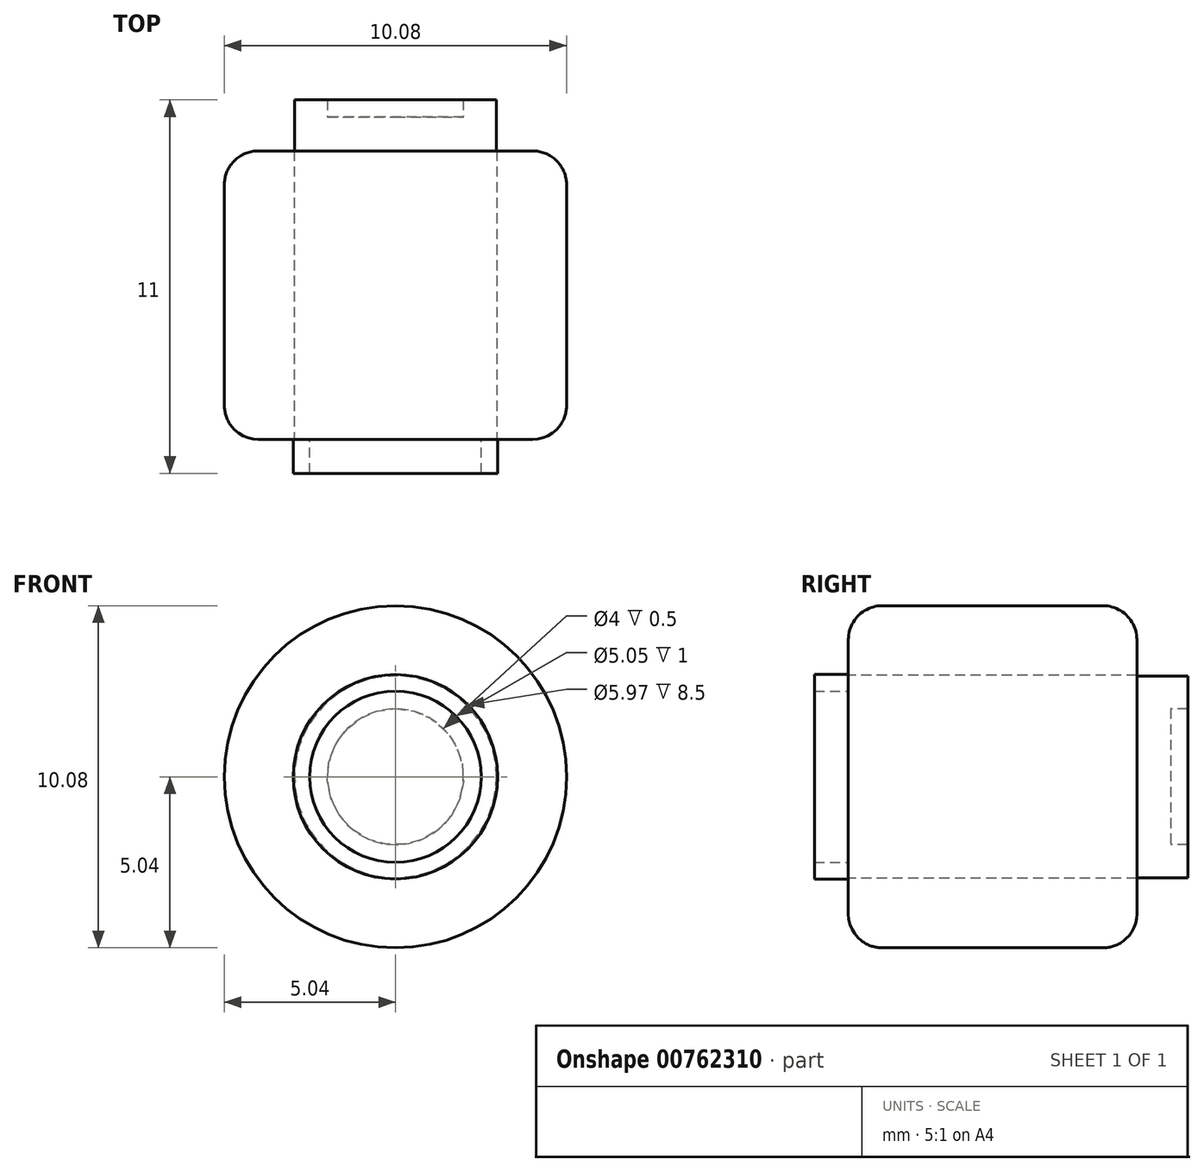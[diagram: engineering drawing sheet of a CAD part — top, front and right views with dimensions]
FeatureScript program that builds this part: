
annotation { "Feature Type Name" : "Feature", "Feature Type Description" : "" }
export const myFeature = defineFeature(function(context is Context, id is Id, definition is map)
    precondition{}
    {
        {
            var Q0;
            Q0=qCreatedBy(makeId("Front.planeOp"),FACE);
            var sketch = newSketch(context, id + "F0", { "sketchPlane" : qUnion([Q0])});
            skCircle(sketch, "E0", {"center": v(0, 0) * mm, "radius": 3.01 * mm});
            skCircle(sketch, "E1", {"center": v(0, 0) * mm, "radius": 2.53 * mm});
            skSolve(sketch);
        }
        {
            var Q0;
            Q0=makeQuery(id+"F0.imprint","IMPRINT",FACE,{"disambiguationData":[TD([[makeQuery(id+"F0.imprint","IMPRINT",EDGE,{"derivedFrom":sQuery(id+"F0.wireOp",EDGE,"E0")}),1.0]])]});
            extrude(context, id + "F1", {"entities" : qUnion([Q0]), "depth" : 1 * mm, "offsetDistance" : 25 * mm});
        }
        {
            var Q0;
            Q0=makeQuery(id+"F1.opExtrude","CAP_FACE",FACE,{"disambiguationData":[OSD([sQuery(id+"F0.wireOp",EDGE,"E0"),sQuery(id+"F0.wireOp",EDGE,"E1")])],"isStart":true});
            var sketch = newSketch(context, id + "F2", { "sketchPlane" : qUnion([Q0])});
            skCircle(sketch, "E2", {"center": v(0, 0) * mm, "radius": 2.99 * mm});
            skCircle(sketch, "E3", {"center": v(0, 0) * mm, "radius": 5.04 * mm});
            skSolve(sketch);
        }
        {
            var Q0;
            Q0 = qSketchRegion(id + "F2", true);
            extrude(context, id + "F3", {"entities" : qUnion([Q0]), "operationType" : NewBodyOperationType.ADD, "depth" : 8.5 * mm, "offsetDistance" : 25 * mm});
        }
        {
            var Q0;
            Q0=makeQuery(id+"F3.opExtrude","CAP_FACE",FACE,{"disambiguationData":[OSD([sQuery(id+"F2.wireOp",EDGE,"E2"),sQuery(id+"F2.wireOp",EDGE,"E3")])],"isStart":false});
            var sketch = newSketch(context, id + "F4", { "sketchPlane" : qUnion([Q0])});
            skCircle(sketch, "E4", {"center": v(0, 0) * mm, "radius": 2.97 * mm});
            skCircle(sketch, "E5", {"center": v(0, 0) * mm, "radius": 2 * mm});
            skSolve(sketch);
        }
        {
            var Q0;
            Q0 = qSketchRegion(id + "F4", true);
            extrude(context, id + "F5", {"entities" : qUnion([Q0]), "depth" : 1.5 * mm, "offsetDistance" : 25 * mm});
        }
        {
            var Q0;
            Q0=makeQuery(id+"F3.opExtrude","CAP_FACE",FACE,{"disambiguationData":[OSD([sQuery(id+"F2.wireOp",EDGE,"E2"),sQuery(id+"F2.wireOp",EDGE,"E3")])],"isStart":false});
            var sketch = newSketch(context, id + "F6", { "sketchPlane" : qUnion([Q0])});
            skCircle(sketch, "E6", {"center": v(0, 0) * mm, "radius": 2 * mm});
            skSolve(sketch);
        }
        {
            var Q0;
            Q0 = qSketchRegion(id + "F6", true);
            extrude(context, id + "F7", {"entities" : qUnion([Q0]), "operationType" : NewBodyOperationType.ADD, "depth" : 1 * mm, "offsetDistance" : 25 * mm});
        }
        {
            var Q0;
            Q0=makeQuery(id+"F3.opExtrude","CAP_EDGE",EDGE,{"disambiguationData":[OSD([sQuery(id+"F2.wireOp",EDGE,"E3")])],"isStart":true});
            fillet(context, id + "F8", {"entities" : qUnion([Q0]), "radius" : 1 * mm, "tangentPropagation" : true, "allowEdgeOverflow" : false});
        }
        {
            var Q0;
            Q0=makeQuery(id+"F3.opExtrude","CAP_EDGE",EDGE,{"disambiguationData":[OSD([sQuery(id+"F2.wireOp",EDGE,"E3")])],"isStart":false});
            fillet(context, id + "F9", {"entities" : qUnion([Q0]), "radius" : 1 * mm, "tangentPropagation" : true, "allowEdgeOverflow" : false});
        }
    });
